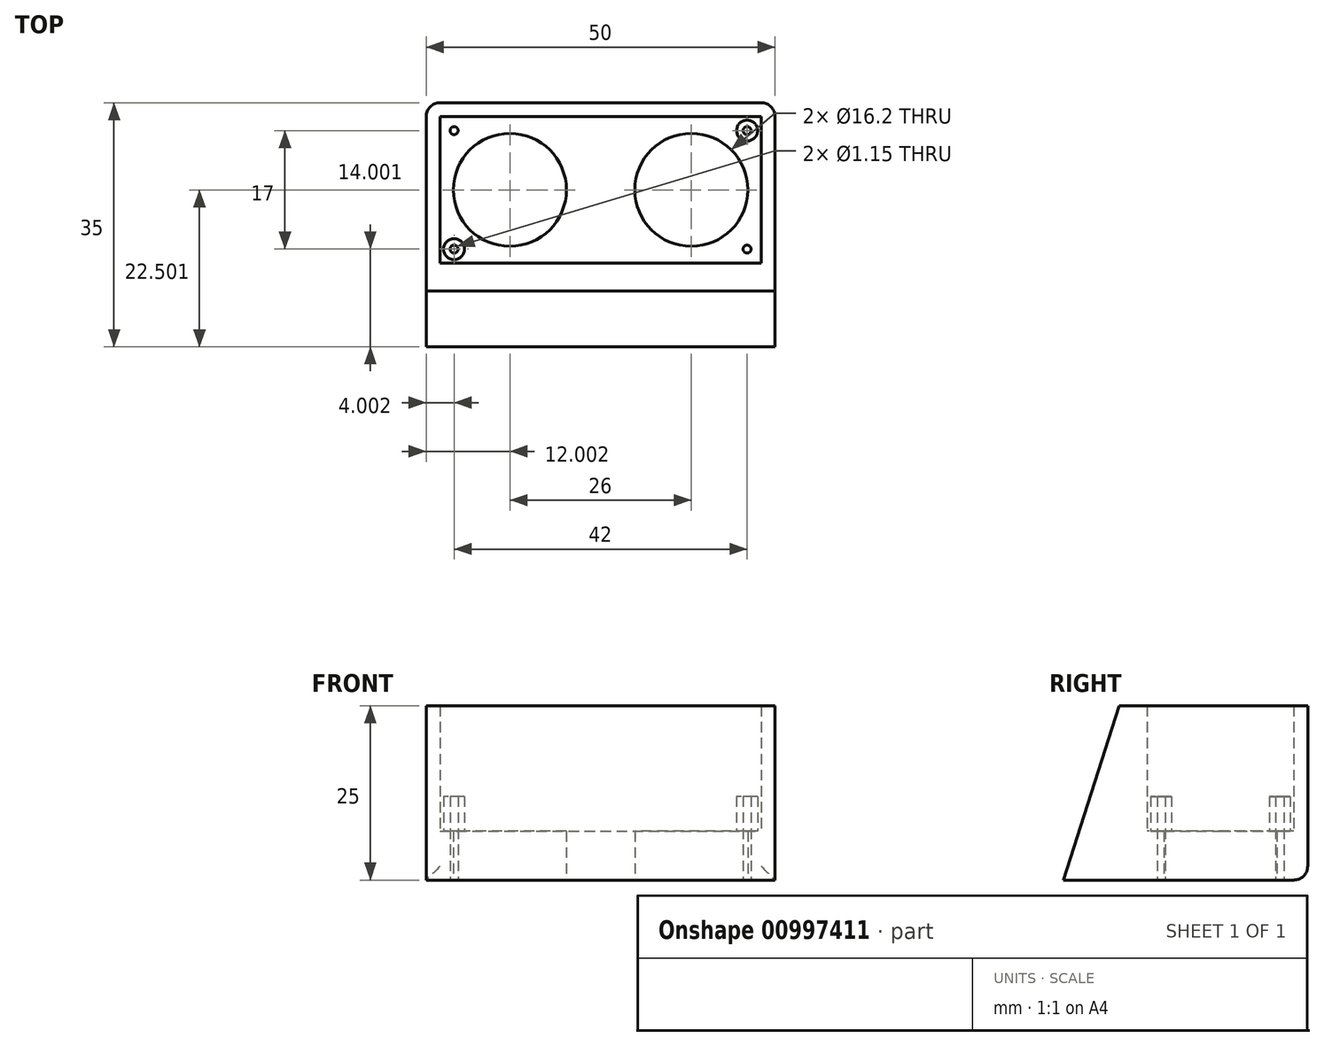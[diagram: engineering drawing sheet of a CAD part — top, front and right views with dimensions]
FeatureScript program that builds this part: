
annotation { "Feature Type Name" : "Feature", "Feature Type Description" : "" }
export const myFeature = defineFeature(function(context is Context, id is Id, definition is map)
    precondition{}
    {
        {
            var Q0;
            Q0=qCreatedBy(makeId("Top.planeOp"),FACE);
            var sketch = newSketch(context, id + "F0", { "sketchPlane" : qUnion([Q0])});
            skLineSegment(sketch, "E0.bottom", {"start": v(-23.07, 5.36) * mm, "end": v(26.93, 5.36) * mm});
            skLineSegment(sketch, "E0.top", {"start": v(-23.07, -19.64) * mm, "end": v(26.93, -19.64) * mm});
            skLineSegment(sketch, "E0.left", {"start": v(-23.07, 5.36) * mm, "end": v(-23.07, -19.64) * mm});
            skLineSegment(sketch, "E0.right", {"start": v(26.93, 5.36) * mm, "end": v(26.93, -19.64) * mm});
            skLineSegment(sketch, "E1", {"start": v(1.93, 5.36) * mm, "end": v(1.93, -19.64) * mm, "construction": true});
            skLineSegment(sketch, "E2", {"start": v(-23.07, -7.14) * mm, "end": v(26.93, -7.14) * mm, "construction": true});
            skCircle(sketch, "E3", {"center": v(-19.07, 1.36) * mm, "radius": 1.5 * mm});
            skCircle(sketch, "E4.MirrorC", {"center": v(22.93, 1.36) * mm, "radius": 1.5 * mm});
            skCircle(sketch, "E5.MirrorC", {"center": v(22.93, -15.64) * mm, "radius": 1.5 * mm});
            skCircle(sketch, "E6.MirrorC", {"center": v(-19.07, -15.64) * mm, "radius": 1.5 * mm});
            skLineSegment(sketch, "E7", {"start": v(-21.07, 5.36) * mm, "end": v(-21.07, -19.64) * mm});
            skLineSegment(sketch, "E8", {"start": v(-21.07, -17.64) * mm, "end": v(26.93, -17.64) * mm});
            skLineSegment(sketch, "E9", {"start": v(24.93, -17.64) * mm, "end": v(24.93, 5.36) * mm});
            skLineSegment(sketch, "E10", {"start": v(24.93, 3.36) * mm, "end": v(-21.07, 3.36) * mm});
            skCircle(sketch, "E11", {"center": v(14.93, -7.14) * mm, "radius": 8.1 * mm});
            skCircle(sketch, "E12.MirrorC", {"center": v(-11.07, -7.14) * mm, "radius": 8.1 * mm});
            skCircle(sketch, "E13", {"center": v(-19.07, 1.36) * mm, "radius": 0.57 * mm});
            skCircle(sketch, "E14.MirrorC", {"center": v(22.93, 1.36) * mm, "radius": 0.57 * mm});
            skCircle(sketch, "E15.MirrorC", {"center": v(-19.07, -15.64) * mm, "radius": 0.57 * mm});
            skCircle(sketch, "E16.MirrorC", {"center": v(22.93, -15.64) * mm, "radius": 0.57 * mm});
            skLineSegment(sketch, "E17.top", {"start": v(-23.07, -29.64) * mm, "end": v(26.93, -29.64) * mm});
            skLineSegment(sketch, "E17.left", {"start": v(-23.07, -19.64) * mm, "end": v(-23.07, -29.64) * mm});
            skLineSegment(sketch, "E17.right", {"start": v(26.93, -19.64) * mm, "end": v(26.93, -29.64) * mm});
            skSolve(sketch);
        }
        {
            var Q0;
            Q0=makeQuery(id+"F0.imprint","IMPRINT",FACE,{"disambiguationData":[TD([[makeQuery(id+"F0.imprint","IMPRINT",EDGE,{"derivedFrom":sQuery(id+"F0.wireOp",EDGE,"E0.bottom")}),-1.0]])]});
            var Q1;
            Q1=makeQuery(id+"F0.imprint","IMPRINT",FACE,{"disambiguationData":[TD([[makeQuery(id+"F0.imprint","IMPRINT",EDGE,{"derivedFrom":sQuery(id+"F0.wireOp",EDGE,"E3")}),1.0]])]});
            var Q2;
            Q2=makeQuery(id+"F0.imprint","IMPRINT",FACE,{"disambiguationData":[TD([[makeQuery(id+"F0.imprint","IMPRINT",EDGE,{"derivedFrom":sQuery(id+"F0.wireOp",EDGE,"E5.MirrorC")}),1.0]])]});
            var Q3;
            Q3=makeQuery(id+"F0.imprint","IMPRINT",FACE,{"disambiguationData":[TD([[makeQuery(id+"F0.imprint","IMPRINT",EDGE,{"derivedFrom":sQuery(id+"F0.wireOp",EDGE,"E4.MirrorC")}),-1.0]])]});
            var Q4;
            Q4=makeQuery(id+"F0.imprint","IMPRINT",FACE,{"disambiguationData":[TD([[makeQuery(id+"F0.imprint","IMPRINT",EDGE,{"derivedFrom":sQuery(id+"F0.wireOp",EDGE,"E6.MirrorC")}),-1.0]])]});
            var Q5;
            Q5=makeQuery(id+"F0.imprint","IMPRINT",FACE,{"disambiguationData":[TD([[makeQuery(id+"F0.imprint","IMPRINT",EDGE,{"derivedFrom":sQuery(id+"F0.wireOp",EDGE,"E3")}),-1.0]])]});
            var Q6;
            {var subQ4=sQuery(id+"F0.wireOp",EDGE,"E0.left");Q6=makeQuery(id+"F0.imprint","IMPRINT",FACE,{"disambiguationData":[TD([[makeQuery(id+"F0.imprint","IMPRINT",EDGE,{"derivedFrom":subQ4}),1.0]])]});}
            var Q7;
            {var subQ4=sQuery(id+"F0.wireOp",EDGE,"E0.right");var subQ5=sQuery(id+"F0.wireOp",EDGE,"E0.top");var subQ6=makeQuery(id+"F0.imprint","INTERSECT",VERTEX,{"derivedFrom":[subQ5,subQ4]});Q7=makeQuery(id+"F0.imprint","IMPRINT",FACE,{"disambiguationData":[TD([[makeQuery(id+"F0.imprint","IMPRINT",EDGE,{"disambiguationData":[TD([[subQ6,1.0]])],"derivedFrom":subQ5}),1.0]])]});}
            var Q8;
            {var subQ1=sQuery(id+"F0.wireOp",EDGE,"E0.right");var subQ5=sQuery(id+"F0.wireOp",EDGE,"E0.bottom");var subQ6=makeQuery(id+"F0.imprint","INTERSECT",VERTEX,{"derivedFrom":[subQ5,subQ1]});Q8=makeQuery(id+"F0.imprint","IMPRINT",FACE,{"disambiguationData":[TD([[makeQuery(id+"F0.imprint","IMPRINT",EDGE,{"disambiguationData":[TD([[subQ6,1.0]])],"derivedFrom":subQ5}),-1.0]])]});}
            extrude(context, id + "F1", {"entities" : qUnion([Q0, Q1, Q2, Q3, Q4, Q5, Q6, Q7, Q8]), "depth" : 2 * mm, "offsetDistance" : 25 * mm});
        }
        {
            var Q0;
            {var subQ4=sQuery(id+"F0.wireOp",EDGE,"E0.left");Q0=makeQuery(id+"F0.imprint","IMPRINT",FACE,{"disambiguationData":[TD([[makeQuery(id+"F0.imprint","IMPRINT",EDGE,{"derivedFrom":subQ4}),1.0]])]});}
            var Q1;
            {var subQ5=sQuery(id+"F0.wireOp",EDGE,"E10");Q1=makeQuery(id+"F0.imprint","IMPRINT",FACE,{"disambiguationData":[TD([[makeQuery(id+"F0.imprint","IMPRINT",EDGE,{"derivedFrom":subQ5}),-1.0]])]});}
            var Q2;
            {var subQ4=sQuery(id+"F0.wireOp",EDGE,"E0.right");var subQ5=sQuery(id+"F0.wireOp",EDGE,"E0.top");var subQ6=makeQuery(id+"F0.imprint","INTERSECT",VERTEX,{"derivedFrom":[subQ5,subQ4]});Q2=makeQuery(id+"F0.imprint","IMPRINT",FACE,{"disambiguationData":[TD([[makeQuery(id+"F0.imprint","IMPRINT",EDGE,{"disambiguationData":[TD([[subQ6,1.0]])],"derivedFrom":subQ5}),1.0]])]});}
            var Q3;
            {var subQ1=sQuery(id+"F0.wireOp",EDGE,"E0.right");var subQ5=sQuery(id+"F0.wireOp",EDGE,"E0.bottom");var subQ6=makeQuery(id+"F0.imprint","INTERSECT",VERTEX,{"derivedFrom":[subQ5,subQ1]});Q3=makeQuery(id+"F0.imprint","IMPRINT",FACE,{"disambiguationData":[TD([[makeQuery(id+"F0.imprint","IMPRINT",EDGE,{"disambiguationData":[TD([[subQ6,1.0]])],"derivedFrom":subQ5}),-1.0]])]});}
            var Q4;
            {var subQ4=sQuery(id+"F0.wireOp",EDGE,"E0.top");var subQ6=sQuery(id+"F0.wireOp",EDGE,"E7");var subQ7=makeQuery(id+"F0.imprint","INTERSECT",VERTEX,{"derivedFrom":[subQ6,subQ4]});Q4=makeQuery(id+"F0.imprint","IMPRINT",FACE,{"disambiguationData":[TD([[makeQuery(id+"F0.imprint","IMPRINT",EDGE,{"disambiguationData":[TD([[subQ7,1.0]])],"derivedFrom":subQ6}),1.0]])]});}
            var Q5;
            Q5=makeQuery(id+"F0.imprint","IMPRINT",FACE,{"disambiguationData":[TD([[makeQuery(id+"F0.imprint","IMPRINT",EDGE,{"derivedFrom":sQuery(id+"F0.wireOp",EDGE,"E17.top")}),1.0]])]});
            extrude(context, id + "F2", {"entities" : qUnion([Q0, Q1, Q2, Q3, Q4, Q5]), "operationType" : NewBodyOperationType.ADD, "depth" : 25 * mm, "offsetDistance" : 25 * mm});
        }
        {
            var Q0;
            Q0=makeQuery(id+"F0.imprint","IMPRINT",FACE,{"disambiguationData":[TD([[makeQuery(id+"F0.imprint","IMPRINT",EDGE,{"derivedFrom":sQuery(id+"F0.wireOp",EDGE,"E3")}),1.0]])]});
            var Q1;
            Q1=makeQuery(id+"F0.imprint","IMPRINT",FACE,{"disambiguationData":[TD([[makeQuery(id+"F0.imprint","IMPRINT",EDGE,{"derivedFrom":sQuery(id+"F0.wireOp",EDGE,"E6.MirrorC")}),-1.0]])]});
            var Q2;
            Q2=makeQuery(id+"F0.imprint","IMPRINT",FACE,{"disambiguationData":[TD([[makeQuery(id+"F0.imprint","IMPRINT",EDGE,{"derivedFrom":sQuery(id+"F0.wireOp",EDGE,"E4.MirrorC")}),-1.0]])]});
            var Q3;
            Q3=makeQuery(id+"F0.imprint","IMPRINT",FACE,{"disambiguationData":[TD([[makeQuery(id+"F0.imprint","IMPRINT",EDGE,{"derivedFrom":sQuery(id+"F0.wireOp",EDGE,"E5.MirrorC")}),1.0]])]});
            extrude(context, id + "F3", {"entities" : qUnion([Q0, Q1, Q2, Q3]), "operationType" : NewBodyOperationType.ADD, "depth" : 7 * mm, "offsetDistance" : 25 * mm});
        }
        {
            var Q0;
            Q0=makeQuery(id+"F0.imprint","IMPRINT",FACE,{"disambiguationData":[TD([[makeQuery(id+"F0.imprint","IMPRINT",EDGE,{"derivedFrom":sQuery(id+"F0.wireOp",EDGE,"E13")}),1.0]])]});
            var Q1;
            Q1=makeQuery(id+"F0.imprint","IMPRINT",FACE,{"disambiguationData":[TD([[makeQuery(id+"F0.imprint","IMPRINT",EDGE,{"derivedFrom":sQuery(id+"F0.wireOp",EDGE,"E15.MirrorC")}),-1.0]])]});
            var Q2;
            Q2=makeQuery(id+"F0.imprint","IMPRINT",FACE,{"disambiguationData":[TD([[makeQuery(id+"F0.imprint","IMPRINT",EDGE,{"derivedFrom":sQuery(id+"F0.wireOp",EDGE,"E16.MirrorC")}),1.0]])]});
            var Q3;
            Q3=makeQuery(id+"F0.imprint","IMPRINT",FACE,{"disambiguationData":[TD([[makeQuery(id+"F0.imprint","IMPRINT",EDGE,{"derivedFrom":sQuery(id+"F0.wireOp",EDGE,"E14.MirrorC")}),-1.0]])]});
            extrude(context, id + "F4", {"entities" : qUnion([Q0, Q1, Q2, Q3]), "operationType" : NewBodyOperationType.ADD, "depth" : 12 * mm, "offsetDistance" : 25 * mm});
        }
        {
            var Q0;
            Q0=makeQuery(id+"F1.opExtrude","CAP_EDGE",EDGE,{"disambiguationData":[OSD([sQuery(id+"F0.wireOp",EDGE,"E0.bottom")])],"isStart":true});
            var Q1;
            {var subQ0=sQuery(id+"F0.wireOp",EDGE,"E0.right");var subQ1=sQuery(id+"F0.wireOp",EDGE,"E0.bottom");Q1=makeQuery(id+"F2.boolean.opBoolean","MERGE",EDGE,{"derivedFrom":[makeQuery(id+"F1.opExtrude","SWEPT_EDGE",EDGE,{"disambiguationData":[OSD([subQ1,subQ0])]}),makeQuery(id+"F2.opExtrude","SWEPT_EDGE",EDGE,{"disambiguationData":[OSD([subQ1,subQ0])]})]});}
            var Q2;
            {var subQ0=sQuery(id+"F0.wireOp",EDGE,"E0.left");var subQ1=sQuery(id+"F0.wireOp",EDGE,"E0.bottom");Q2=makeQuery(id+"F2.boolean.opBoolean","MERGE",EDGE,{"derivedFrom":[makeQuery(id+"F1.opExtrude","SWEPT_EDGE",EDGE,{"disambiguationData":[OSD([subQ1,subQ0])]}),makeQuery(id+"F2.opExtrude","SWEPT_EDGE",EDGE,{"disambiguationData":[OSD([subQ1,subQ0])]})]});}
            fillet(context, id + "F5", {"entities" : qUnion([Q0, Q1, Q2]), "radius" : 2 * mm, "tangentPropagation" : true, "allowEdgeOverflow" : false});
        }
        {
            var Q0;
            {var subQ0=sQuery(id+"F0.wireOp",EDGE,"E0.right");Q0=makeQuery(id+"F2.boolean.opBoolean","MERGE",FACE,{"derivedFrom":[makeQuery(id+"F1.opExtrude","SWEPT_FACE",FACE,{"disambiguationData":[OSD([subQ0])]}),makeQuery(id+"F2.opExtrude","SWEPT_FACE",FACE,{"disambiguationData":[OSD([subQ0,sQuery(id+"F0.wireOp",EDGE,"E17.right")])]})]});}
            var sketch = newSketch(context, id + "F6", { "sketchPlane" : qUnion([Q0])});
            skLineSegment(sketch, "E18", {"start": v(-21.64, 25) * mm, "end": v(-29.64, 0) * mm});
            skSolve(sketch);
        }
        {
            var Q0;
            {var subQ0=sQuery(id+"F6.wireOp",EDGE,"E18");Q0=makeQuery(id+"F6.imprint","IMPRINT",FACE,{"disambiguationData":[TD([[makeQuery(id+"F6.imprint","IMPRINT",EDGE,{"derivedFrom":subQ0}),-1.0]])]});}
            extrude(context, id + "F7", {"entities" : qUnion([Q0]), "operationType" : NewBodyOperationType.REMOVE, "oppositeDirection" : true, "depth" : 52 * mm, "offsetDistance" : 25 * mm});
        }
    });
